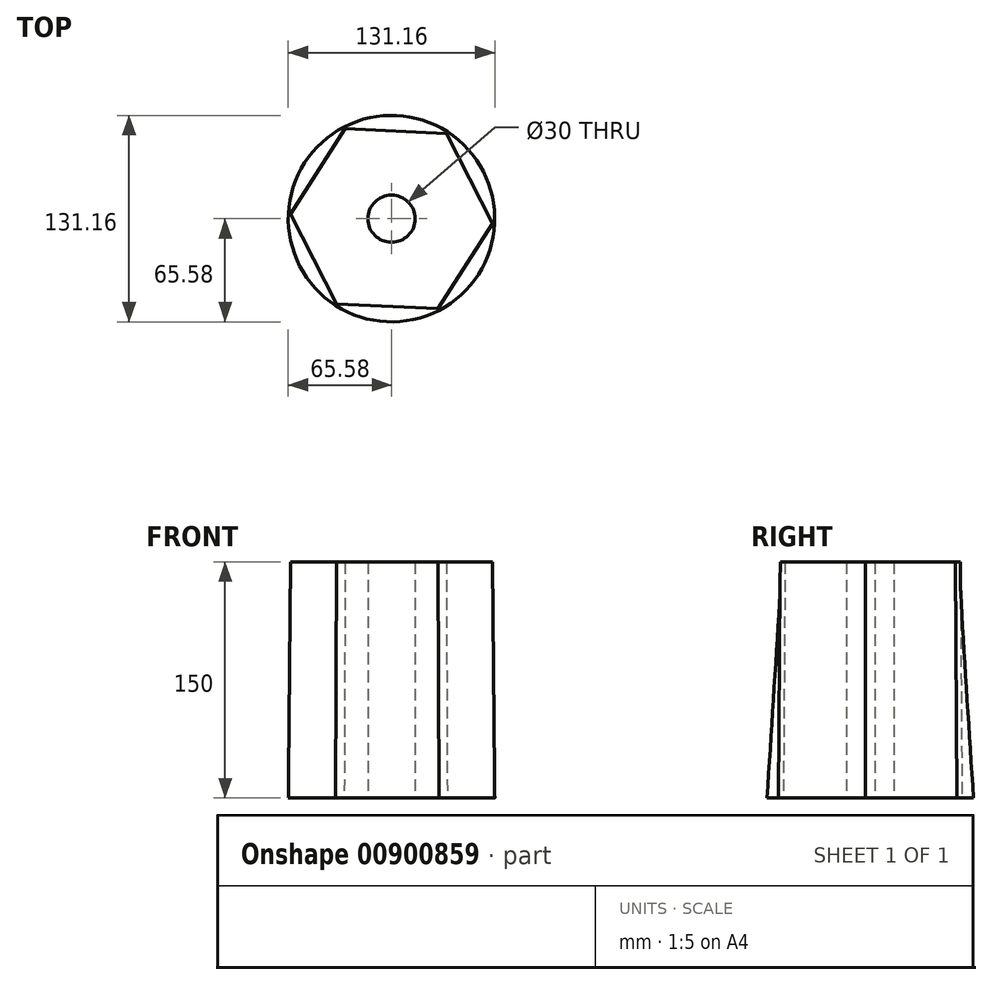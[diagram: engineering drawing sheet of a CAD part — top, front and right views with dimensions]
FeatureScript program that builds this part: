
annotation { "Feature Type Name" : "Feature", "Feature Type Description" : "" }
export const myFeature = defineFeature(function(context is Context, id is Id, definition is map)
    precondition{}
    {
        {
            var Q0;
            Q0=qCreatedBy(makeId("Top.planeOp"),FACE);
            cPlane(context, id + "F0", {"entities" : qUnion([Q0]), "cplaneType" : CPlaneType.OFFSET, "offset" : 150 * mm, "width" : 150 * mm, "height" : 150 * mm});
        }
        {
            var Q0;
            Q0=qCreatedBy(makeId("Top.planeOp"),FACE);
            var sketch = newSketch(context, id + "F1", { "sketchPlane" : qUnion([Q0])});
            skCircle(sketch, "E0", {"center": v(0, 0) * mm, "radius": 65.58 * mm});
            skSolve(sketch);
        }
        {
            var Q0;
            Q0=qCreatedBy(id+"F0.planeOp",FACE);
            var sketch = newSketch(context, id + "F2", { "sketchPlane" : qUnion([Q0])});
            skCircle(sketch, "E1.cCircle", {"center": v(0, 0) * mm, "radius": 55.72 * mm, "construction": true});
            skLineSegment(sketch, "E1.0", {"start": v(64.27, -3.06) * mm, "end": v(29.48, -57.2) * mm});
            skLineSegment(sketch, "E1.1", {"start": v(29.48, -57.2) * mm, "end": v(-34.79, -54.13) * mm});
            skLineSegment(sketch, "E1.2", {"start": v(-34.79, -54.13) * mm, "end": v(-64.27, 3.06) * mm});
            skLineSegment(sketch, "E1.3", {"start": v(-64.27, 3.06) * mm, "end": v(-29.48, 57.2) * mm});
            skLineSegment(sketch, "E1.4", {"start": v(-29.48, 57.2) * mm, "end": v(34.79, 54.13) * mm});
            skLineSegment(sketch, "E1.5", {"start": v(34.79, 54.13) * mm, "end": v(64.27, -3.06) * mm});
            skPoint(sketch, "E1.0.midPoint", {"position": v(46.88, -30.13) * mm});
            skSolve(sketch);
        }
        {
            var Q0;
            Q0=makeQuery(id+"F2.imprint","IMPRINT",FACE,{"disambiguationData":[TD([[makeQuery(id+"F2.imprint","IMPRINT",EDGE,{"derivedFrom":sQuery(id+"F2.wireOp",EDGE,"E1.0")}),-1.0]])]});
            var Q1;
            Q1=makeQuery(id+"F1.imprint","IMPRINT",FACE,{"disambiguationData":[TD([[makeQuery(id+"F1.imprint","IMPRINT",EDGE,{"derivedFrom":sQuery(id+"F1.wireOp",EDGE,"E0")}),1.0]])]});
            loft(context, id + "F3", {"sheetProfilesArray" : [{ "sheetProfileEntities" : qUnion([Q0]) }, { "sheetProfileEntities" : qUnion([Q1]) }]});
        }
        {
            var Q0;
            Q0=makeQuery(id+"F3.opLoft","CAP_FACE",FACE,{"disambiguationData":[OSD([makeQuery(id+"F1.imprint","IMPRINT",FACE,{"disambiguationData":[TD([[makeQuery(id+"F1.imprint","IMPRINT",EDGE,{"derivedFrom":sQuery(id+"F1.wireOp",EDGE,"E0")}),1.0]])]})])],"isStart":true});
            var sketch = newSketch(context, id + "F4", { "sketchPlane" : qUnion([Q0])});
            skCircle(sketch, "E2", {"center": v(0, 0) * mm, "radius": 15 * mm});
            skSolve(sketch);
        }
        {
            var Q0;
            Q0 = qSketchRegion(id + "F4", true);
            extrude(context, id + "F5", {"entities" : qUnion([Q0]), "operationType" : NewBodyOperationType.REMOVE, "oppositeDirection" : true, "depth" : 208 * mm, "offsetDistance" : 25 * mm});
        }
    });
